# Revit family: 4cff909f-02df-4cd1-a322-b8c992ae452f
name_source: partatom
category: Furniture
revit_build: Autodesk Revit 2016 (Build: 20161004_0715(x64)
units: mm (PartAtom-declared; Revit-internal decimal feet)

## family parameters
Cut with Voids When Loaded = No
Host = Face
OmniClass Number = 23.40.95.17.17
OmniClass Title = Mirrors
Room Calculation Point = No
Shared = No

## types (1)
- 18 x 24 Ligature Resistant Wood Framed Mirror
    Default Elevation = 54"
    Depth = 1 1/8"
    Description = Ligature Resistant Wood Framed Mirror
    Frame Finish = Wood-BSP-Cherry
    Height = 24"
    Manufacturer = Behavioral Safety Products
    Model = FM160
    Product Documentation Link = http://besafeprod.com
    Product Page URL = http://besafeprod.com
    Product data url = https://bimobject.com
    Type Image = <None>
    URL = http://besafeprod.com
    Unit Size = 22 5/8W x 28 5/8H
    Width = 18"

## geometry (parser evidence)
native form markers: Blend x22, Sweep x3
no freeform markers — native parametric forms only
